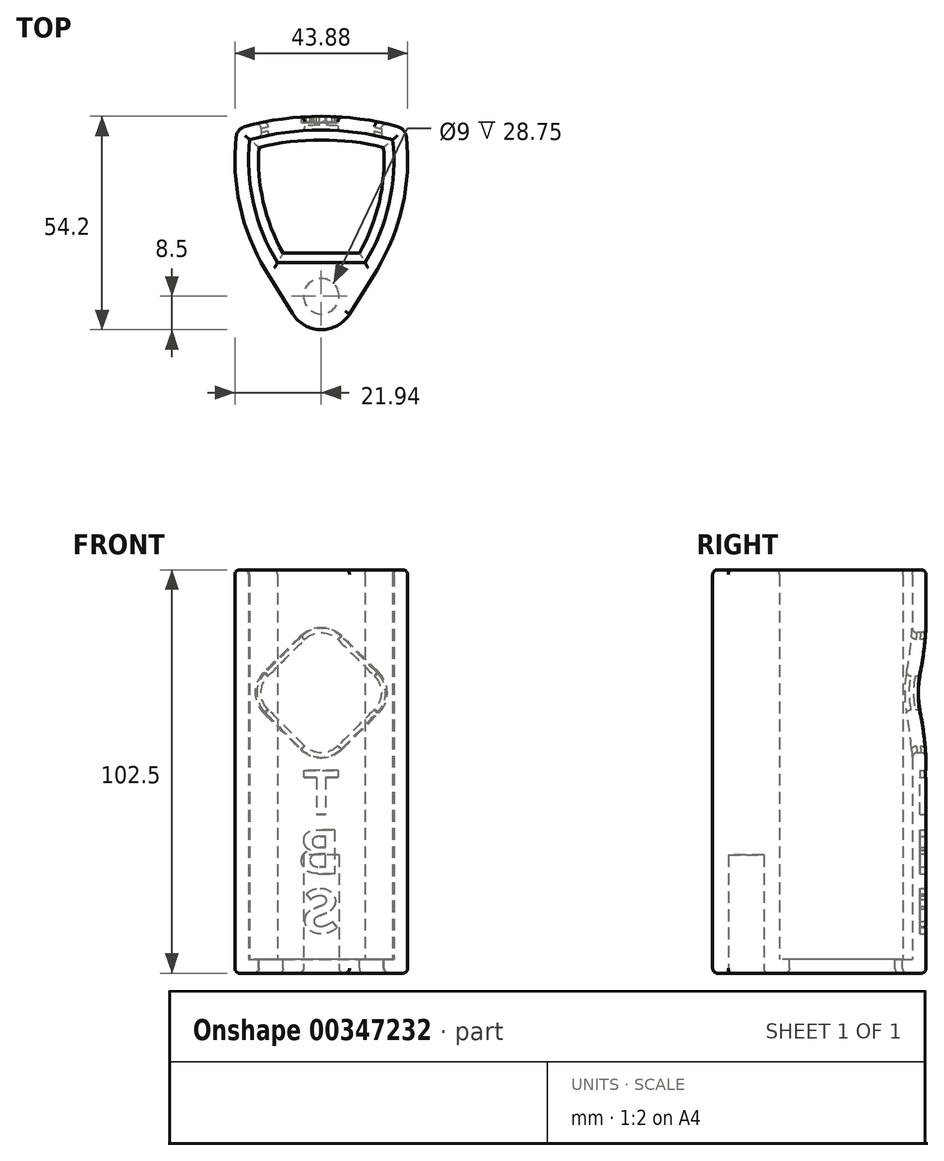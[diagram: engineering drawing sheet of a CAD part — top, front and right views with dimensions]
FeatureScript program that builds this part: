
annotation { "Feature Type Name" : "Feature", "Feature Type Description" : "" }
export const myFeature = defineFeature(function(context is Context, id is Id, definition is map)
    precondition{}
    {
        {
            var Q0;
            Q0=qCreatedBy(makeId("Top.planeOp"),FACE);
            var sketch = newSketch(context, id + "F0", { "sketchPlane" : qUnion([Q0])});
            skLineSegment(sketch, "E0", {"start": v(0, 0) * mm, "end": v(11.12, 0) * mm});
            skLineSegment(sketch, "E1", {"start": v(11.12, 0) * mm, "end": v(-11.12, 0) * mm});
            skArc(sketch, "E2", {"start": v(-18.16, 31.28) * mm, "mid": v(-17.22, 15.06) * mm, "end": v(-11.13, 0) * mm});
            skArc(sketch, "E3", {"start": v(11.13, 0) * mm, "mid": v(17.22, 15.06) * mm, "end": v(18.16, 31.28) * mm});
            skArc(sketch, "E4", {"start": v(18.16, 31.28) * mm, "mid": v(0, 33.7) * mm, "end": v(-18.16, 31.28) * mm});
            skArc(sketch, "E5.0", {"start": v(-21.34, 34) * mm, "mid": v(-20.88, 15.46) * mm, "end": v(-14.11, -1.82) * mm});
            skArc(sketch, "E5.1", {"start": v(21.34, 34) * mm, "mid": v(0, 37.2) * mm, "end": v(-21.34, 34) * mm});
            skArc(sketch, "E5.2", {"start": v(14.11, -1.82) * mm, "mid": v(20.88, 15.46) * mm, "end": v(21.34, 34) * mm});
            skCircle(sketch, "E6", {"center": v(0, -8.5) * mm, "radius": 4.5 * mm});
            skLineSegment(sketch, "E7", {"start": v(-14.11, -1.82) * mm, "end": v(-7.23, -12.97) * mm});
            skLineSegment(sketch, "E8", {"start": v(7.19, -13.03) * mm, "end": v(14.11, -1.82) * mm});
            skArc(sketch, "E9", {"start": v(-7.23, -12.97) * mm, "mid": v(-0.04, -17) * mm, "end": v(7.19, -13.03) * mm});
            skLineSegment(sketch, "E10", {"start": v(21.34, 34) * mm, "end": v(21.34, 39.15) * mm});
            skLineSegment(sketch, "E11", {"start": v(21.34, 39.15) * mm, "end": v(-21.34, 39.15) * mm});
            skLineSegment(sketch, "E12", {"start": v(-21.34, 39.15) * mm, "end": v(-21.34, 34) * mm});
            skSolve(sketch);
        }
        {
            var Q0;
            {var subQ3=sQuery(id+"F0.wireOp",EDGE,"E2");Q0=makeQuery(id+"F0.imprint","IMPRINT",FACE,{"disambiguationData":[TD([[makeQuery(id+"F0.imprint","IMPRINT",EDGE,{"derivedFrom":subQ3}),-1.0]])]});}
            var Q1;
            Q1=makeQuery(id+"F0.imprint","IMPRINT",FACE,{"disambiguationData":[TD([[makeQuery(id+"F0.imprint","IMPRINT",EDGE,{"derivedFrom":sQuery(id+"F0.wireOp",EDGE,"E6")}),1.0]])]});
            extrude(context, id + "F1", {"entities" : qUnion([Q0, Q1]), "depth" : 102.5 * mm});
        }
        {
            var Q0;
            {var subQ1=sQuery(id+"F0.wireOp",EDGE,"E2");Q0=makeQuery(id+"F0.imprint","IMPRINT",FACE,{"disambiguationData":[TD([[makeQuery(id+"F0.imprint","IMPRINT",EDGE,{"derivedFrom":subQ1}),1.0]])]});}
            extrude(context, id + "F2", {"entities" : qUnion([Q0]), "operationType" : NewBodyOperationType.ADD, "depth" : 3.5 * mm});
        }
        {
            var Q0;
            Q0=makeQuery(id+"F0.imprint","IMPRINT",FACE,{"disambiguationData":[TD([[makeQuery(id+"F0.imprint","IMPRINT",EDGE,{"derivedFrom":sQuery(id+"F0.wireOp",EDGE,"E6")}),1.0]])]});
            extrude(context, id + "F3", {"entities" : qUnion([Q0]), "operationType" : NewBodyOperationType.REMOVE, "depth" : 30 * mm});
        }
        {
            var Q0;
            Q0=makeQuery(id+"F0.imprint","IMPRINT",FACE,{"disambiguationData":[TD([[makeQuery(id+"F0.imprint","IMPRINT",EDGE,{"derivedFrom":sQuery(id+"F0.wireOp",EDGE,"E5.1")}),-1.0]])]});
            extrude(context, id + "F4", {"entities" : qUnion([Q0]), "operationType" : NewBodyOperationType.ADD, "depth" : 102.5 * mm});
        }
        {
            var Q0;
            Q0=makeQuery(id+"F4.opExtrude","SWEPT_FACE",FACE,{"disambiguationData":[OSD([sQuery(id+"F0.wireOp",EDGE,"E11")])]});
            var sketch = newSketch(context, id + "F5", { "sketchPlane" : qUnion([Q0])});
            skPoint(sketch, "E13.endSnap0", {"position": v(0, 0) * mm});
            skLineSegment(sketch, "E14", {"start": v(-17.75, 71.25) * mm, "end": v(0, 89) * mm});
            skLineSegment(sketch, "E15", {"start": v(17.75, 71.25) * mm, "end": v(0, 53.5) * mm});
            skLineSegment(sketch, "E16", {"start": v(0, 53.5) * mm, "end": v(-17.75, 71.25) * mm});
            skLineSegment(sketch, "E17", {"start": v(0, 89) * mm, "end": v(17.75, 71.25) * mm});
            skSolve(sketch);
        }
        {
            var Q0;
            Q0=makeQuery(id+"F5.imprint","IMPRINT",FACE,{"disambiguationData":[TD([[makeQuery(id+"F5.imprint","IMPRINT",EDGE,{"derivedFrom":sQuery(id+"F5.wireOp",EDGE,"E14")}),-1.0]])]});
            extrude(context, id + "F6", {"entities" : qUnion([Q0]), "operationType" : NewBodyOperationType.REMOVE, "oppositeDirection" : true, "depth" : 10 * mm});
        }
        {
            var Q0;
            Q0=makeQuery(id+"F6.boolean.opBoolean","COPY",EDGE,{"derivedFrom":makeQuery(id+"F6.opExtrude","SWEPT_EDGE",EDGE,{"disambiguationData":[OSD([sQuery(id+"F5.wireOp",EDGE,"E15"),sQuery(id+"F5.wireOp",EDGE,"E17")])]})});
            var Q1;
            Q1=makeQuery(id+"F6.boolean.opBoolean","COPY",EDGE,{"derivedFrom":makeQuery(id+"F6.opExtrude","SWEPT_EDGE",EDGE,{"disambiguationData":[OSD([sQuery(id+"F5.wireOp",EDGE,"E15"),sQuery(id+"F5.wireOp",EDGE,"E16")])]})});
            var Q2;
            Q2=makeQuery(id+"F6.boolean.opBoolean","COPY",EDGE,{"derivedFrom":makeQuery(id+"F6.opExtrude","SWEPT_EDGE",EDGE,{"disambiguationData":[OSD([sQuery(id+"F5.wireOp",EDGE,"E14"),sQuery(id+"F5.wireOp",EDGE,"E16")])]})});
            var Q3;
            Q3=makeQuery(id+"F6.boolean.opBoolean","COPY",EDGE,{"derivedFrom":makeQuery(id+"F6.opExtrude","SWEPT_EDGE",EDGE,{"disambiguationData":[OSD([sQuery(id+"F5.wireOp",EDGE,"E14"),sQuery(id+"F5.wireOp",EDGE,"E17")])]})});
            fillet(context, id + "F7", {"entities" : qUnion([Q0, Q1, Q2, Q3]), "radius" : 6 * mm, "tangentPropagation" : true, "allowEdgeOverflow" : false});
        }
        {
            var Q0;
            Q0=makeQuery(id+"F4.opExtrude","SWEPT_FACE",FACE,{"disambiguationData":[OSD([sQuery(id+"F0.wireOp",EDGE,"E11")])]});
            var sketch = newSketch(context, id + "F8", { "sketchPlane" : qUnion([Q0])});
            skText(sketch, "E18", { "text": "T\nB\nS", "fontName": "NotoSansCJKsc-Bold.otf"});
            skPoint(sketch, "E18.firstSnap0", {"position": v(-21.34, 51.25) * mm});
            const initialGuessF8  = {"E18": [-0.00469, 0.04038, 1, 0, 0.01087]};
            skSetInitialGuess(sketch, initialGuessF8);
            skSolve(sketch);
        }
        {
            var Q0;
            Q0 = qSketchRegion(id + "F8", true);
            extrude(context, id + "F9", {"entities" : qUnion([Q0]), "operationType" : NewBodyOperationType.REMOVE, "oppositeDirection" : true, "depth" : 4 * mm});
        }
        {
            var Q0;
            Q0=makeQuery(id+"F0.imprint","IMPRINT",FACE,{"disambiguationData":[TD([[makeQuery(id+"F0.imprint","IMPRINT",EDGE,{"derivedFrom":sQuery(id+"F0.wireOp",EDGE,"E5.1")}),-1.0]])]});
            extrude(context, id + "F10", {"entities" : qUnion([Q0]), "operationType" : NewBodyOperationType.REMOVE, "depth" : 102.5 * mm});
        }
        {
            var Q0;
            Q0=makeQuery(id+"F9.boolean.opBoolean","COPY",FACE,{"derivedFrom":makeQuery(id+"F9.opExtrude","CAP_FACE",FACE,{"disambiguationData":[OSD([sQuery(id+"F8.wireOp",EDGE,"E18.sketch_text.stroke-0"),sQuery(id+"F8.wireOp",EDGE,"E18.sketch_text.stroke-1"),sQuery(id+"F8.wireOp",EDGE,"E18.sketch_text.stroke-2"),sQuery(id+"F8.wireOp",EDGE,"E18.sketch_text.stroke-3"),sQuery(id+"F8.wireOp",EDGE,"E18.sketch_text.stroke-4"),sQuery(id+"F8.wireOp",EDGE,"E18.sketch_text.stroke-5"),sQuery(id+"F8.wireOp",EDGE,"E18.sketch_text.stroke-6"),sQuery(id+"F8.wireOp",EDGE,"E18.sketch_text.stroke-7")])],"isStart":false})});
            var Q1;
            Q1=makeQuery(id+"F9.boolean.opBoolean","COPY",FACE,{"derivedFrom":makeQuery(id+"F9.opExtrude","CAP_FACE",FACE,{"disambiguationData":[OSD([sQuery(id+"F8.wireOp",EDGE,"E18.sketch_text.stroke-8"),sQuery(id+"F8.wireOp",EDGE,"E18.sketch_text.stroke-9"),sQuery(id+"F8.wireOp",EDGE,"E18.sketch_text.stroke-10"),sQuery(id+"F8.wireOp",EDGE,"E18.sketch_text.stroke-11"),sQuery(id+"F8.wireOp",EDGE,"E18.sketch_text.stroke-12"),sQuery(id+"F8.wireOp",EDGE,"E18.sketch_text.stroke-13"),sQuery(id+"F8.wireOp",EDGE,"E18.sketch_text.stroke-14"),sQuery(id+"F8.wireOp",EDGE,"E18.sketch_text.stroke-15"),sQuery(id+"F8.wireOp",EDGE,"E18.sketch_text.stroke-16"),sQuery(id+"F8.wireOp",EDGE,"E18.sketch_text.stroke-17"),sQuery(id+"F8.wireOp",EDGE,"E18.sketch_text.stroke-18"),sQuery(id+"F8.wireOp",EDGE,"E18.sketch_text.stroke-19"),sQuery(id+"F8.wireOp",EDGE,"E18.sketch_text.stroke-20"),sQuery(id+"F8.wireOp",EDGE,"E18.sketch_text.stroke-21"),sQuery(id+"F8.wireOp",EDGE,"E18.sketch_text.stroke-22"),sQuery(id+"F8.wireOp",EDGE,"E18.sketch_text.stroke-23"),sQuery(id+"F8.wireOp",EDGE,"E18.sketch_text.stroke-24"),sQuery(id+"F8.wireOp",EDGE,"E18.sketch_text.stroke-25")])],"isStart":false})});
            var Q2;
            Q2=makeQuery(id+"F9.boolean.opBoolean","COPY",FACE,{"derivedFrom":makeQuery(id+"F9.opExtrude","CAP_FACE",FACE,{"disambiguationData":[OSD([sQuery(id+"F8.wireOp",EDGE,"E18.sketch_text.stroke-26"),sQuery(id+"F8.wireOp",EDGE,"E18.sketch_text.stroke-27"),sQuery(id+"F8.wireOp",EDGE,"E18.sketch_text.stroke-28"),sQuery(id+"F8.wireOp",EDGE,"E18.sketch_text.stroke-29"),sQuery(id+"F8.wireOp",EDGE,"E18.sketch_text.stroke-30"),sQuery(id+"F8.wireOp",EDGE,"E18.sketch_text.stroke-31"),sQuery(id+"F8.wireOp",EDGE,"E18.sketch_text.stroke-32"),sQuery(id+"F8.wireOp",EDGE,"E18.sketch_text.stroke-33"),sQuery(id+"F8.wireOp",EDGE,"E18.sketch_text.stroke-34"),sQuery(id+"F8.wireOp",EDGE,"E18.sketch_text.stroke-35"),sQuery(id+"F8.wireOp",EDGE,"E18.sketch_text.stroke-36"),sQuery(id+"F8.wireOp",EDGE,"E18.sketch_text.stroke-37"),sQuery(id+"F8.wireOp",EDGE,"E18.sketch_text.stroke-38"),sQuery(id+"F8.wireOp",EDGE,"E18.sketch_text.stroke-39"),sQuery(id+"F8.wireOp",EDGE,"E18.sketch_text.stroke-40"),sQuery(id+"F8.wireOp",EDGE,"E18.sketch_text.stroke-41")])],"isStart":false})});
            extrude(context, id + "F11", {"entities" : qUnion([Q0, Q1, Q2]), "operationType" : NewBodyOperationType.ADD, "depth" : .5 * mm});
        }
        {
            var Q0;
            {var subQ0=sQuery(id+"F0.wireOp",EDGE,"E12");var subQ1=sQuery(id+"F0.wireOp",EDGE,"E5.1");var subQ2=sQuery(id+"F0.wireOp",EDGE,"E5.0");Q0=makeQuery(id+"F10.boolean.opBoolean","MERGE",EDGE,{"derivedFrom":[makeQuery(id+"F4.boolean.opBoolean","MERGE",EDGE,{"derivedFrom":[makeQuery(id+"F1.opExtrude","SWEPT_EDGE",EDGE,{"disambiguationData":[OSD([subQ2,subQ1,subQ0])]}),makeQuery(id+"F4.opExtrude","SWEPT_EDGE",EDGE,{"disambiguationData":[OSD([subQ2,subQ1,subQ0])]})]}),makeQuery(id+"F10.opExtrude","SWEPT_EDGE",EDGE,{"disambiguationData":[OSD([subQ2,subQ1,subQ0])]})]});}
            var Q1;
            {var subQ0=sQuery(id+"F0.wireOp",EDGE,"E10");var subQ1=sQuery(id+"F0.wireOp",EDGE,"E5.2");var subQ2=sQuery(id+"F0.wireOp",EDGE,"E5.1");Q1=makeQuery(id+"F10.boolean.opBoolean","MERGE",EDGE,{"derivedFrom":[makeQuery(id+"F4.boolean.opBoolean","MERGE",EDGE,{"derivedFrom":[makeQuery(id+"F1.opExtrude","SWEPT_EDGE",EDGE,{"disambiguationData":[OSD([subQ2,subQ1,subQ0])]}),makeQuery(id+"F4.opExtrude","SWEPT_EDGE",EDGE,{"disambiguationData":[OSD([subQ2,subQ1,subQ0])]})]}),makeQuery(id+"F10.opExtrude","SWEPT_EDGE",EDGE,{"disambiguationData":[OSD([subQ2,subQ1,subQ0])]})]});}
            fillet(context, id + "F12", {"entities" : qUnion([Q0, Q1]), "radius" : 3 * mm, "tangentPropagation" : true, "allowEdgeOverflow" : false});
        }
        {
            var Q0;
            Q0=makeQuery(id+"F2.opExtrude","CAP_FACE",FACE,{"disambiguationData":[OSD([sQuery(id+"F0.wireOp",EDGE,"E1"),sQuery(id+"F0.wireOp",EDGE,"E2"),sQuery(id+"F0.wireOp",EDGE,"E3"),sQuery(id+"F0.wireOp",EDGE,"E4")])],"isStart":false});
            var sketch = newSketch(context, id + "F13", { "sketchPlane" : qUnion([Q0])});
            skArc(sketch, "E19.0", {"start": v(9.7, 2.5) * mm, "mid": v(14.75, 15.45) * mm, "end": v(15.83, 29.3) * mm});
            skLineSegment(sketch, "E19.1", {"start": v(-9.7, 2.5) * mm, "end": v(9.7, 2.5) * mm});
            skArc(sketch, "E19.2", {"start": v(-15.83, 29.3) * mm, "mid": v(-14.75, 15.45) * mm, "end": v(-9.7, 2.5) * mm});
            skArc(sketch, "E19.3", {"start": v(15.83, 29.3) * mm, "mid": v(0, 31.2) * mm, "end": v(-15.83, 29.3) * mm});
            skSolve(sketch);
        }
        {
            var Q0;
            Q0=makeQuery(id+"F13.imprint","IMPRINT",FACE,{"disambiguationData":[TD([[makeQuery(id+"F13.imprint","IMPRINT",EDGE,{"derivedFrom":sQuery(id+"F13.wireOp",EDGE,"E19.0")}),1.0]])]});
            extrude(context, id + "F14", {"entities" : qUnion([Q0]), "operationType" : NewBodyOperationType.REMOVE, "oppositeDirection" : true, "depth" : 25 * mm});
        }
        {
            var Q0;
            {var subQ0=sQuery(id+"F0.wireOp",EDGE,"E5.1");var subQ1=sQuery(id+"F0.wireOp",EDGE,"E4");var subQ2=sQuery(id+"F0.wireOp",EDGE,"E3");var subQ3=sQuery(id+"F0.wireOp",EDGE,"E2");var subQ4=sQuery(id+"F0.wireOp",EDGE,"E1");Q0=makeQuery(id+"F4.boolean.opBoolean","MERGE",FACE,{"derivedFrom":[makeQuery(id+"F2.boolean.opBoolean","MERGE",FACE,{"derivedFrom":[makeQuery(id+"F1.opExtrude","CAP_FACE",FACE,{"disambiguationData":[OSD([subQ4,subQ3,subQ2,subQ1,sQuery(id+"F0.wireOp",EDGE,"E5.0"),subQ0,sQuery(id+"F0.wireOp",EDGE,"E5.2"),sQuery(id+"F0.wireOp",EDGE,"E7"),sQuery(id+"F0.wireOp",EDGE,"E8"),sQuery(id+"F0.wireOp",EDGE,"E9")])],"isStart":true}),makeQuery(id+"F2.opExtrude","CAP_FACE",FACE,{"disambiguationData":[OSD([subQ4,subQ3,subQ2,subQ1])],"isStart":true})]}),makeQuery(id+"F4.opExtrude","CAP_FACE",FACE,{"disambiguationData":[OSD([subQ0,sQuery(id+"F0.wireOp",EDGE,"E10"),sQuery(id+"F0.wireOp",EDGE,"E11"),sQuery(id+"F0.wireOp",EDGE,"E12")])],"isStart":true})]});}
            fillet(context, id + "F15", {"entities" : qUnion([Q0]), "radius" : 1.25 * mm, "tangentPropagation" : true, "allowEdgeOverflow" : false});
        }
        {
            var Q0;
            {var subQ0=sQuery(id+"F0.wireOp",EDGE,"E5.1");Q0=makeQuery(id+"F4.boolean.opBoolean","MERGE",FACE,{"derivedFrom":[makeQuery(id+"F1.opExtrude","CAP_FACE",FACE,{"disambiguationData":[OSD([sQuery(id+"F0.wireOp",EDGE,"E1"),sQuery(id+"F0.wireOp",EDGE,"E2"),sQuery(id+"F0.wireOp",EDGE,"E3"),sQuery(id+"F0.wireOp",EDGE,"E4"),sQuery(id+"F0.wireOp",EDGE,"E5.0"),subQ0,sQuery(id+"F0.wireOp",EDGE,"E5.2"),sQuery(id+"F0.wireOp",EDGE,"E7"),sQuery(id+"F0.wireOp",EDGE,"E8"),sQuery(id+"F0.wireOp",EDGE,"E9")])],"isStart":false}),makeQuery(id+"F4.opExtrude","CAP_FACE",FACE,{"disambiguationData":[OSD([subQ0,sQuery(id+"F0.wireOp",EDGE,"E10"),sQuery(id+"F0.wireOp",EDGE,"E11"),sQuery(id+"F0.wireOp",EDGE,"E12")])],"isStart":false})]});}
            fillet(context, id + "F16", {"entities" : qUnion([Q0]), "radius" : 1.25 * mm, "tangentPropagation" : true, "allowEdgeOverflow" : false});
        }
        {
            var Q0;
            Q0=makeQuery(id+"F10.boolean.opBoolean","INTERSECT",EDGE,{"derivedFrom":[makeQuery(id+"F7.opFillet","BLEND_FACE",FACE,{"disambiguationData":[OSD([sQuery(id+"F5.wireOp",EDGE,"E15"),sQuery(id+"F5.wireOp",EDGE,"E17")])]}),makeQuery(id+"F10.opExtrude","SWEPT_FACE",FACE,{"disambiguationData":[OSD([sQuery(id+"F0.wireOp",EDGE,"E5.1")])]})]});
            var Q1;
            Q1=makeQuery(id+"F7.opFillet","BLEND_EDGE",EDGE,{"blendedFrom":[makeQuery(id+"F6.boolean.opBoolean","COPY",EDGE,{"derivedFrom":makeQuery(id+"F6.opExtrude","SWEPT_EDGE",EDGE,{"disambiguationData":[OSD([sQuery(id+"F5.wireOp",EDGE,"E15"),sQuery(id+"F5.wireOp",EDGE,"E17")])]})}),makeQuery(id+"F1.opExtrude","SWEPT_FACE",FACE,{"disambiguationData":[OSD([sQuery(id+"F0.wireOp",EDGE,"E4")])]})],"blendedInto":[makeQuery(id+"F1.opExtrude","SWEPT_FACE",FACE,{"disambiguationData":[OSD([sQuery(id+"F0.wireOp",EDGE,"E4")])]})]});
            fillet(context, id + "F17", {"entities" : qUnion([Q0, Q1]), "radius" : 1.25 * mm, "tangentPropagation" : true, "allowEdgeOverflow" : false});
        }
    });
